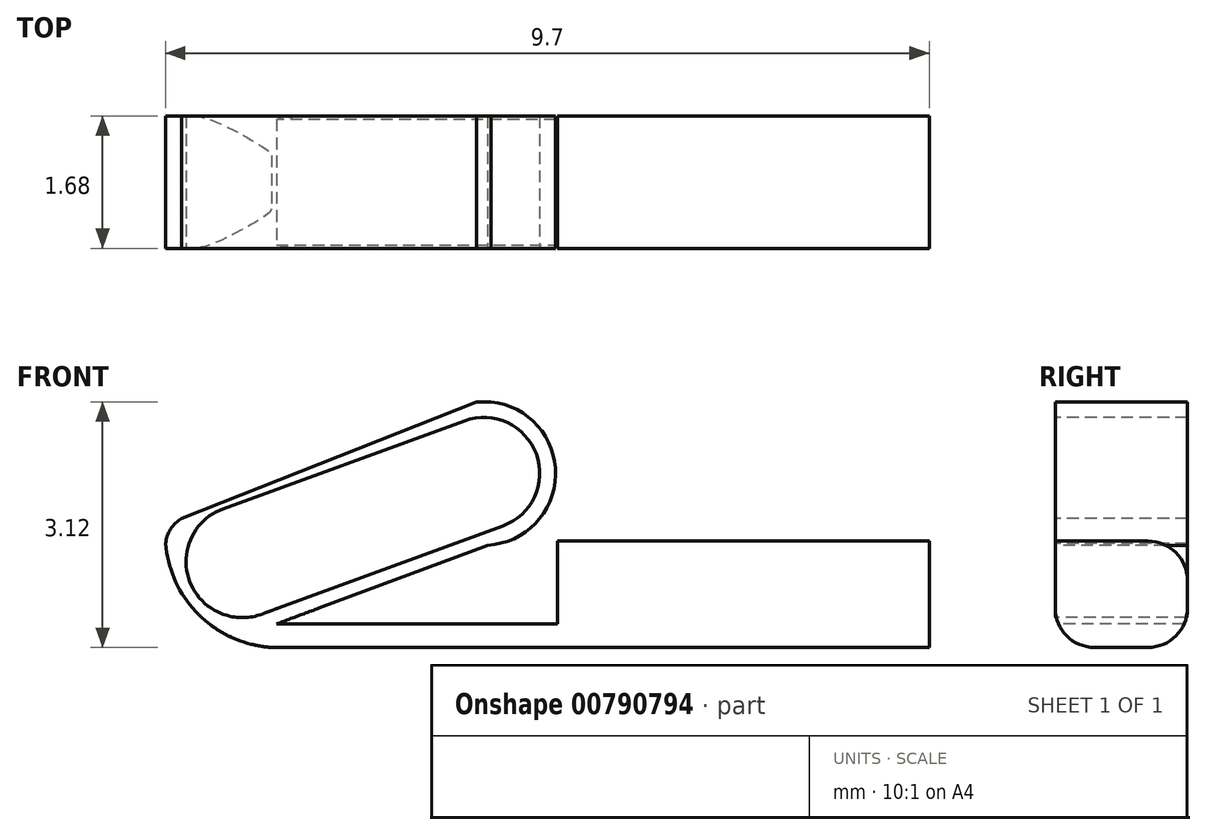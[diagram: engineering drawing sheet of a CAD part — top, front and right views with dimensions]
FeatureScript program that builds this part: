
annotation { "Feature Type Name" : "Feature", "Feature Type Description" : "" }
export const myFeature = defineFeature(function(context is Context, id is Id, definition is map)
    precondition{}
    {
        {
            var Q0;
            Q0=qCreatedBy(makeId("Top.planeOp"),FACE);
            var sketch = newSketch(context, id + "F0", { "sketchPlane" : qUnion([Q0])});
            skLineSegment(sketch, "E0.bottom", {"start": v(4.85, 0.84) * mm, "end": v(-4.85, 0.84) * mm});
            skLineSegment(sketch, "E0.top", {"start": v(4.85, -0.84) * mm, "end": v(-4.85, -0.84) * mm});
            skLineSegment(sketch, "E0.left", {"start": v(4.85, 0.84) * mm, "end": v(4.85, -0.84) * mm});
            skLineSegment(sketch, "E0.right", {"start": v(-4.85, 0.84) * mm, "end": v(-4.85, -0.84) * mm});
            skPoint(sketch, "E0.middle", {"position": v(0, 0) * mm});
            skSolve(sketch);
        }
        {
            var Q0;
            Q0=makeQuery(id+"F0.imprint","IMPRINT",FACE,{"disambiguationData":[TD([[makeQuery(id+"F0.imprint","IMPRINT",EDGE,{"derivedFrom":sQuery(id+"F0.wireOp",EDGE,"E0.bottom")}),1.0]])]});
            extrude(context, id + "F1", {"entities" : qUnion([Q0]), "depth" : 3.12 * mm, "offsetDistance" : 25 * mm});
        }
        {
            var Q0;
            Q0=makeQuery(id+"F1.opExtrude","SWEPT_FACE",FACE,{"disambiguationData":[OSD([sQuery(id+"F0.wireOp",EDGE,"E0.top")])]});
            var sketch = newSketch(context, id + "F2", { "sketchPlane" : qUnion([Q0])});
            skLineSegment(sketch, "E1.bottom", {"start": v(4.85, 0) * mm, "end": v(0.13, 0) * mm});
            skLineSegment(sketch, "E1.top", {"start": v(4.85, 1.35) * mm, "end": v(0.13, 1.35) * mm});
            skLineSegment(sketch, "E1.left", {"start": v(4.85, 0) * mm, "end": v(4.85, 1.35) * mm});
            skLineSegment(sketch, "E1.right", {"start": v(0.13, 0) * mm, "end": v(0.13, 1.35) * mm});
            skPoint(sketch, "E2.first.point", {"position": v(-4.85, 1.56) * mm});
            skPoint(sketch, "E2.second.point", {"position": v(-3.32, 0) * mm});
            skPoint(sketch, "E2.third.point", {"position": v(-1.98, 1.3) * mm});
            skArc(sketch, "E3.0", {"start": v(-3.44, 0.3) * mm, "mid": v(-3.41, 0.3) * mm, "end": v(-3.38, 0.3) * mm});
            skLineSegment(sketch, "E4", {"start": v(-3.32, 0) * mm, "end": v(0.13, 0) * mm});
            skLineSegment(sketch, "E5", {"start": v(-3.44, 0.3) * mm, "end": v(0.13, 0.3) * mm});
            skArc(sketch, "E6", {"start": v(-0.76, 1.3) * mm, "mid": v(0.1, 2.28) * mm, "end": v(-0.9, 3.12) * mm});
            skPoint(sketch, "E6.first.point", {"position": v(-0.9, 3.12) * mm});
            skPoint(sketch, "E6.second.point", {"position": v(-0.76, 1.3) * mm});
            skPoint(sketch, "E6.third.point", {"position": v(-1.72, 2.13) * mm});
            skLineSegment(sketch, "E7", {"start": v(-4.65, 1.64) * mm, "end": v(-0.9, 3.12) * mm});
            skLineSegment(sketch, "E8", {"start": v(-0.76, 1.3) * mm, "end": v(-3.44, 0.3) * mm});
            skArc(sketch, "E9.trimOffspring", {"start": v(-4.85, 1.32) * mm, "mid": v(-4.36, 0.35) * mm, "end": v(-3.32, 0) * mm});
            skArc(sketch, "E10", {"start": v(-4.65, 1.64) * mm, "mid": v(-4.78, 1.5) * mm, "end": v(-4.85, 1.32) * mm});
            skSolve(sketch);
        }
        {
            var Q0;
            {var subQ0=sQuery(id+"F2.wireOp",EDGE,"E7");Q0=makeQuery(id+"F2.imprint","IMPRINT",FACE,{"disambiguationData":[TD([[makeQuery(id+"F2.imprint","IMPRINT",EDGE,{"derivedFrom":subQ0}),1.0]])]});}
            var Q1;
            {var subQ4=sQuery(id+"F2.wireOp",EDGE,"E1.top");Q1=makeQuery(id+"F2.imprint","IMPRINT",FACE,{"disambiguationData":[TD([[makeQuery(id+"F2.imprint","IMPRINT",EDGE,{"derivedFrom":subQ4}),-1.0]])]});}
            var Q2;
            {var subQ0=sQuery(id+"F2.wireOp",EDGE,"E9.trimOffspring");var subQ1=sQuery(id+"F0.wireOp",EDGE,"E0.top");var subQ4=makeQuery(id+"F1.opExtrude","CAP_EDGE",EDGE,{"disambiguationData":[OSD([subQ1])],"isStart":true});var subQ5=makeQuery(id+"F2.imprint","INTERSECT",VERTEX,{"derivedFrom":[subQ4,subQ0]});Q2=makeQuery(id+"F2.imprint","IMPRINT",FACE,{"disambiguationData":[TD([[makeQuery(id+"F2.imprint","IMPRINT",EDGE,{"disambiguationData":[TD([[subQ5,1.0]])],"derivedFrom":subQ0}),-1.0]])]});}
            extrude(context, id + "F3", {"entities" : qUnion([Q0, Q1, Q2]), "operationType" : NewBodyOperationType.REMOVE, "endBound" : BoundingType.THROUGH_ALL, "oppositeDirection" : true, "depth" : 25 * mm, "offsetDistance" : 25 * mm});
        }
        {
            var Q0;
            Q0=makeQuery(id+"F3.boolean.opBoolean","COPY",EDGE,{"derivedFrom":makeQuery(id+"F3.opExtrude","CAP_EDGE",EDGE,{"disambiguationData":[OSD([sQuery(id+"F2.wireOp",EDGE,"E1.top")])],"isStart":true})});
            var Q1;
            Q1=makeQuery(id+"F3.boolean.opBoolean","INTERSECT",EDGE,{"derivedFrom":[makeQuery(id+"F1.opExtrude","SWEPT_FACE",FACE,{"disambiguationData":[OSD([sQuery(id+"F0.wireOp",EDGE,"E0.bottom")])]}),makeQuery(id+"F3.opExtrude","SWEPT_FACE",FACE,{"disambiguationData":[OSD([sQuery(id+"F2.wireOp",EDGE,"E1.top")])]})]});
            var Q2;
            Q2=makeQuery(id+"F1.opExtrude","CAP_EDGE",EDGE,{"disambiguationData":[OSD([sQuery(id+"F0.wireOp",EDGE,"E0.bottom")])],"isStart":true});
            var Q3;
            Q3=makeQuery(id+"F1.opExtrude","CAP_EDGE",EDGE,{"disambiguationData":[OSD([sQuery(id+"F0.wireOp",EDGE,"E0.top")])],"isStart":true});
            fillet(context, id + "F4", {"entities" : qUnion([Q0, Q1, Q2, Q3]), "radius" : .5 * mm, "tangentPropagation" : true, "allowEdgeOverflow" : false});
        }
        {
            var Q0;
            Q0=makeQuery(id+"F4.opFillet","SPLIT",FACE,{"disambiguationData":[OD(0.0)],"derivedFrom":makeQuery(id+"F1.opExtrude","SWEPT_FACE",FACE,{"disambiguationData":[OSD([sQuery(id+"F0.wireOp",EDGE,"E0.top")])]})});
            var sketch = newSketch(context, id + "F5", { "sketchPlane" : qUnion([Q0])});
            skArc(sketch, "E11", {"start": v(-0.56, 1.54) * mm, "mid": v(-0.14, 2.45) * mm, "end": v(-1.05, 2.88) * mm});
            skArc(sketch, "E12", {"start": v(-4.12, 1.76) * mm, "mid": v(-4.55, 0.85) * mm, "end": v(-3.63, 0.42) * mm});
            skLineSegment(sketch, "E13", {"start": v(-4.12, 1.76) * mm, "end": v(-1.05, 2.88) * mm});
            skLineSegment(sketch, "E14", {"start": v(-0.56, 1.54) * mm, "end": v(-3.63, 0.42) * mm});
            skSolve(sketch);
        }
        {
            var Q0;
            {var subQ1=sQuery(id+"F5.wireOp",EDGE,"E11");Q0=makeQuery(id+"F5.imprint","IMPRINT",FACE,{"disambiguationData":[TD([[makeQuery(id+"F5.imprint","IMPRINT",EDGE,{"derivedFrom":subQ1}),1.0]])]});}
            extrude(context, id + "F6", {"entities" : qUnion([Q0]), "operationType" : NewBodyOperationType.REMOVE, "endBound" : BoundingType.THROUGH_ALL, "oppositeDirection" : true, "depth" : 25 * mm, "offsetDistance" : 25 * mm});
        }
    });
